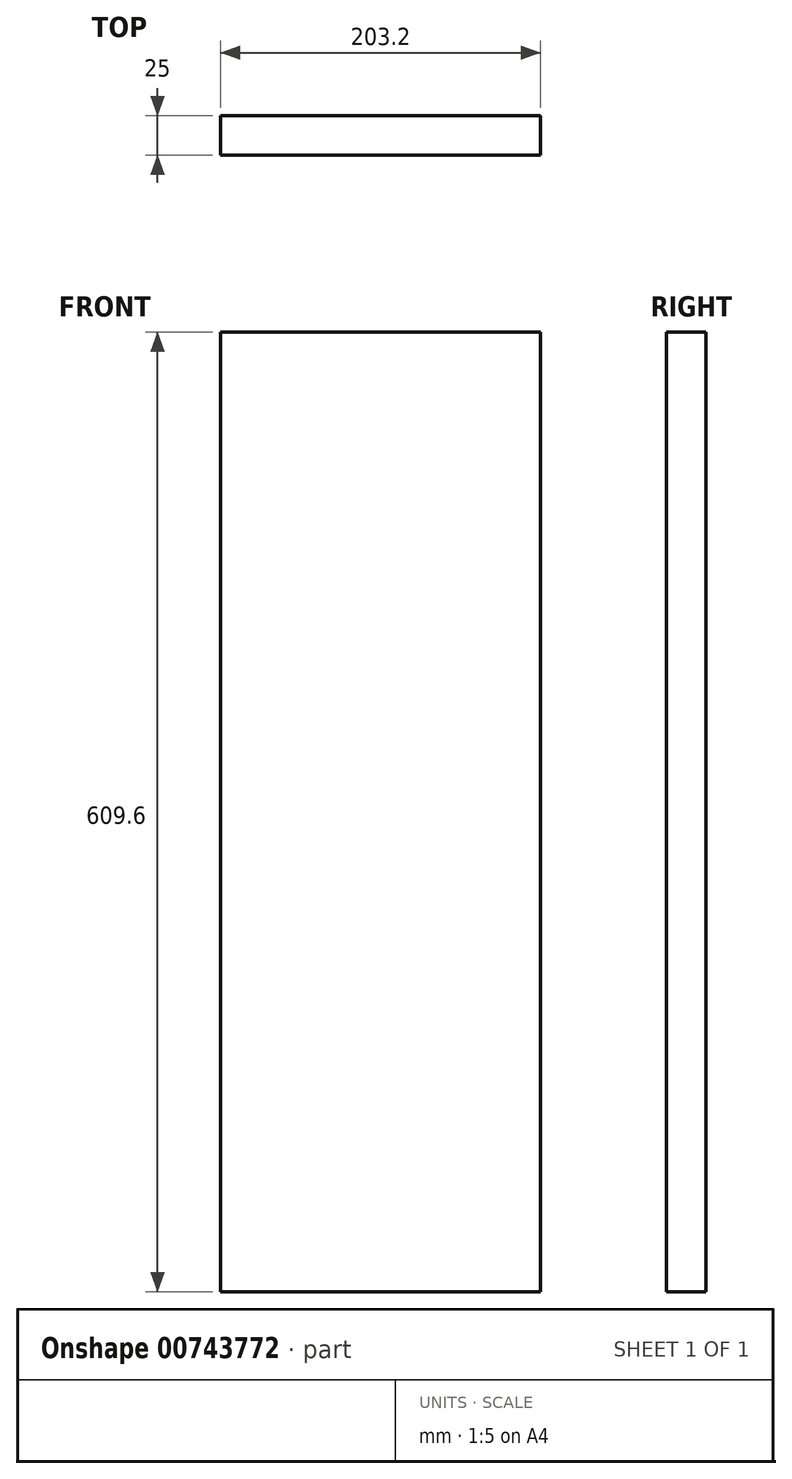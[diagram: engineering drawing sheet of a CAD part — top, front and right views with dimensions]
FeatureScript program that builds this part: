
annotation { "Feature Type Name" : "Feature", "Feature Type Description" : "" }
export const myFeature = defineFeature(function(context is Context, id is Id, definition is map)
    precondition{}
    {
        {
            var Q0;
            Q0=qCreatedBy(makeId("Front.planeOp"),FACE);
            var sketch = newSketch(context, id + "F0", { "sketchPlane" : qUnion([Q0])});
            skLineSegment(sketch, "E0.bottom", {"start": v(-156.34, 270.37) * mm, "end": v(46.86, 270.37) * mm});
            skLineSegment(sketch, "E0.top", {"start": v(-156.34, -339.23) * mm, "end": v(46.86, -339.23) * mm});
            skLineSegment(sketch, "E0.left", {"start": v(-156.34, 270.37) * mm, "end": v(-156.34, -339.23) * mm});
            skLineSegment(sketch, "E0.right", {"start": v(46.86, 270.37) * mm, "end": v(46.86, -339.23) * mm});
            skSolve(sketch);
        }
        {
            var Q0;
            Q0 = qSketchRegion(id + "F0", true);
            extrude(context, id + "F1", {"entities" : qUnion([Q0]), "oppositeDirection" : true, "depth" : 25 * mm, "offsetDistance" : 25 * mm});
        }
    });
